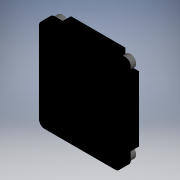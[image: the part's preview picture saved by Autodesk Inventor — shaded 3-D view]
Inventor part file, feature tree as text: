
AUTODESK INVENTOR PART (.ipt)
format: ipt  version: 2017.3 (Build 213256000, 256)  size: 340,480 bytes
history: native  units: mm (DEFAULTED — no unit token found)
features: other x35, sketch x10, extrude x7, pattern_linear x3, revolve x2, hole x1
ambient origin geometry x8: Origin, YZ Plane, XZ Plane, XY Plane, X Axis, Y Axis, Z Axis, Center Point
bodies: Solid1 (feature_tree)
feature tree (58):
  extrude  "Extrusion1"  Depth=7.5mm TaperAngle=0.0deg
  extrude  "Extrusion2"  Depth=5.0mm TaperAngle=0.0deg
  extrude  "Extrusion3"  Depth=20.0mm
  extrude  "Extrusion4"  Depth=20.0mm
  revolve  "Revolution1"  [1 undecoded]
  pattern_linear  "Rectangular Pattern1"  Spacing1=0.0mm  [1 undecoded]
  extrude  "Extrusion5"  TaperAngle=0.0deg  [1 undecoded]
  pattern_linear  "Rectangular Pattern2"  Spacing1=0.0mm  [1 undecoded]
  hole  "Hole1"  [1 undecoded]
  pattern_linear  "Rectangular Pattern3"  [2 undecoded]
  revolve  "Revolution2"  [1 undecoded]
  extrude  "Extrusion6"  [1 undecoded]
  extrude  "Extrusion7"  [1 undecoded]
  other  "geh_XY"
  other  "geh_YZ"
  other  "geh_ZX"
  other  "geh_X"
  other  "geh_Y"
  other  "geh_Z"
  other  "geh_Center"
  other  "ring_XY"
  other  "ring_YZ"
  other  "ring_ZX"
  other  "ring_X"
  other  "ring_Y"
  other  "ring_Z"
  other  "ring_Center"
  other  "typenschild_XY"
  other  "typenschild_YZ"
  other  "typenschild_ZX"
  other  "typenschild_X"
  other  "typenschild_Y"
  other  "typenschild_Z"
  other  "typenschild_Center"
  other  "vss1_XY"
  other  "vss1_YZ"
  other  "vss1_ZX"
  other  "vss1_X"
  other  "vss1_Y"
  other  "vss1_Z"
  other  "vss1_Center"
  other  "vss2_XY"
  other  "vss2_YZ"
  other  "vss2_ZX"
  other  "vss2_X"
  other  "vss2_Y"
  other  "vss2_Z"
  other  "vss2_Center"
  sketch  "Sketch_1"  dims[d0=15.0mm d1=0.0mm d2=7.5mm d3=0.0mm]
  sketch  "Sketch_2"  dims[d4=120.0mm d5=0.0mm d6=5.0mm d7=0.0mm]
  sketch  "Sketch_3"  dims[d8=360.0deg d9=20.0mm d11=50.0mm d12=20.0mm d14=58.0mm]
  sketch  "Sketch_4"  dims[d15=2.5mm d16=0.0mm d17=20.0mm d19=50.0mm d20=20.0mm d22=58.0mm]
  sketch  "Sketch_5"  dims[d23=5.91747mm d24=6.1mm d25=10.0mm d26=0.1mm d27=90.0deg d28=7.325366mm d29=20.594885mm d30=20.0mm d32=20.396078mm d33=10.0mm d35=0.0mm]
  sketch  "Sketch_7"  dims[d36=360.0deg]
  sketch  "Sketch7"  dims[d37=1.0mm d38=0.0mm]
  sketch  "Sketch_11"  dims[d39=0.7mm d40=0.0mm]
  sketch  "Sketch_12"  dims[d41=0.0mm]
  sketch  "Sketch_15"  dims[d42=0.0mm d43=0.0mm d44=0.0mm d45=0.0mm]
note: 10 required parameter values undecoded (feature->parameter linkage not recoverable at this tier; creation-order binding heuristic only, values carry confidence <= 0.55)